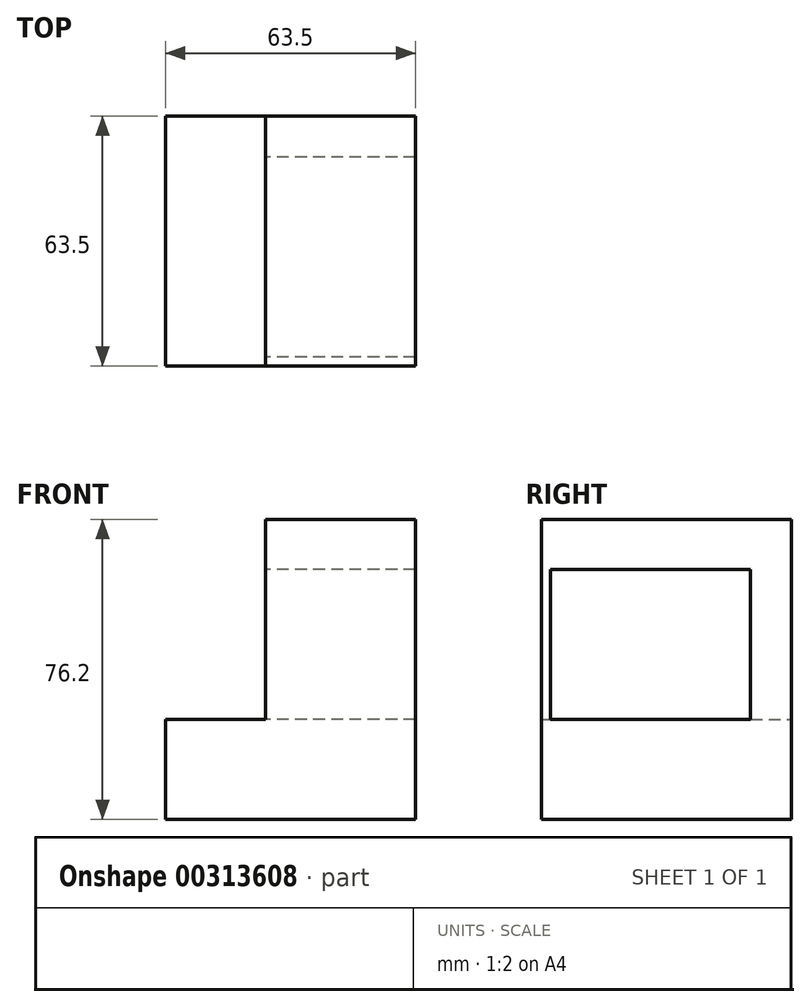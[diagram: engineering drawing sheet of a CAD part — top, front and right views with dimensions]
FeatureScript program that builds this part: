
annotation { "Feature Type Name" : "Feature", "Feature Type Description" : "" }
export const myFeature = defineFeature(function(context is Context, id is Id, definition is map)
    precondition{}
    {
        {
            var Q0;
            Q0=qCreatedBy(makeId("Front.planeOp"),FACE);
            var sketch = newSketch(context, id + "F0", { "sketchPlane" : qUnion([Q0])});
            skLineSegment(sketch, "E0", {"start": v(-34.02, -55.33) * mm, "end": v(29.48, -55.33) * mm});
            skLineSegment(sketch, "E1", {"start": v(29.48, -55.33) * mm, "end": v(29.48, 20.87) * mm});
            skLineSegment(sketch, "E2", {"start": v(29.48, 20.87) * mm, "end": v(-8.62, 20.87) * mm});
            skLineSegment(sketch, "E3", {"start": v(-34.02, -55.33) * mm, "end": v(-34.02, -29.93) * mm});
            skLineSegment(sketch, "E4", {"start": v(-34.02, -29.93) * mm, "end": v(-8.62, -29.93) * mm});
            skLineSegment(sketch, "E5", {"start": v(-8.62, 20.87) * mm, "end": v(-8.62, -29.93) * mm});
            skSolve(sketch);
        }
        {
            var Q0;
            Q0=makeQuery(id+"F0.imprint","IMPRINT",FACE,{"disambiguationData":[TD([[makeQuery(id+"F0.imprint","IMPRINT",EDGE,{"derivedFrom":sQuery(id+"F0.wireOp",EDGE,"E0")}),1.0]])]});
            extrude(context, id + "F1", {"entities" : qUnion([Q0]), "depth" : 63.5 * mm});
        }
        {
            var Q0;
            Q0=makeQuery(id+"F1.opExtrude","SWEPT_FACE",FACE,{"disambiguationData":[OSD([sQuery(id+"F0.wireOp",EDGE,"E5")])]});
            var sketch = newSketch(context, id + "F2", { "sketchPlane" : qUnion([Q0])});
            skLineSegment(sketch, "E6", {"start": v(61.16, -29.93) * mm, "end": v(10.36, -29.93) * mm});
            skLineSegment(sketch, "E7", {"start": v(61.16, -29.93) * mm, "end": v(61.16, 8.17) * mm});
            skLineSegment(sketch, "E8", {"start": v(61.16, 8.17) * mm, "end": v(10.36, 8.17) * mm});
            skLineSegment(sketch, "E9", {"start": v(10.36, 8.17) * mm, "end": v(10.36, -29.93) * mm});
            skSolve(sketch);
        }
        {
            var Q0;
            Q0=makeQuery(id+"F2.imprint","IMPRINT",FACE,{"disambiguationData":[TD([[makeQuery(id+"F2.imprint","IMPRINT",EDGE,{"derivedFrom":sQuery(id+"F2.wireOp",EDGE,"E6")}),-1.0]])]});
            extrude(context, id + "F3", {"entities" : qUnion([Q0]), "operationType" : NewBodyOperationType.REMOVE, "oppositeDirection" : true, "depth" : 50.8 * mm});
        }
    });
